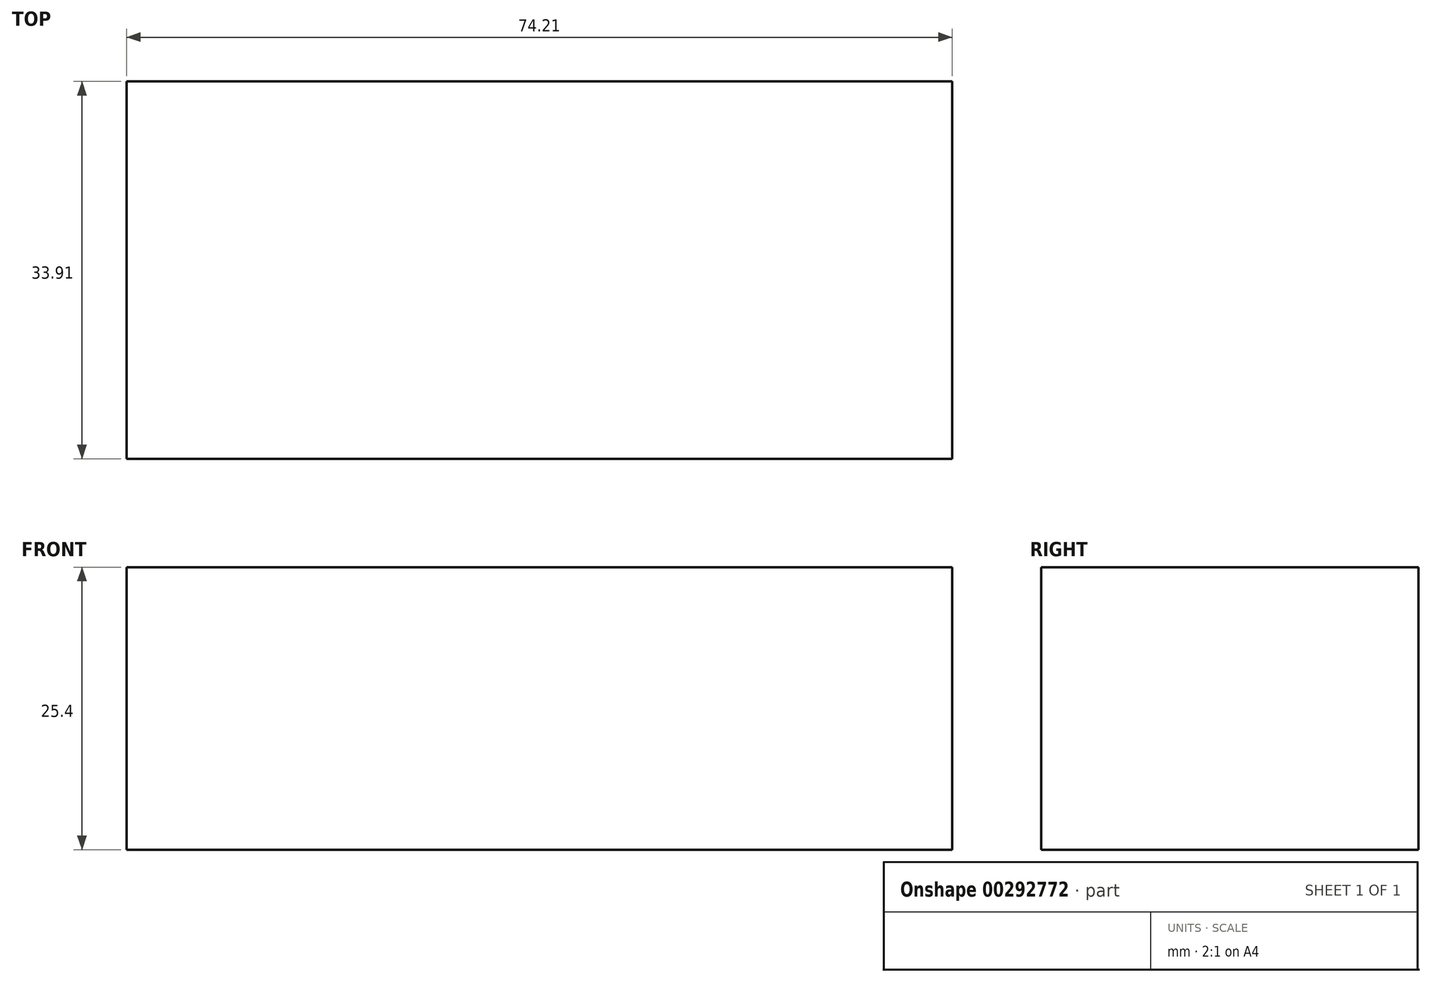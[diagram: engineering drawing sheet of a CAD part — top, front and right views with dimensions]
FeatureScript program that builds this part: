
annotation { "Feature Type Name" : "Feature", "Feature Type Description" : "" }
export const myFeature = defineFeature(function(context is Context, id is Id, definition is map)
    precondition{}
    {
        {
            var Q0;
            Q0=qCreatedBy(makeId("Top.planeOp"),FACE);
            var sketch = newSketch(context, id + "F0", { "sketchPlane" : qUnion([Q0])});
            skLineSegment(sketch, "E0.bottom", {"start": v(-23.48, -15.07) * mm, "end": v(50.73, -15.07) * mm});
            skLineSegment(sketch, "E0.top", {"start": v(-23.48, 18.84) * mm, "end": v(50.73, 18.84) * mm});
            skLineSegment(sketch, "E0.left", {"start": v(-23.48, -15.07) * mm, "end": v(-23.48, 18.84) * mm});
            skLineSegment(sketch, "E0.right", {"start": v(50.73, -15.07) * mm, "end": v(50.73, 18.84) * mm});
            skSolve(sketch);
        }
        {
            var Q0;
            Q0 = qSketchRegion(id + "F0", true);
            extrude(context, id + "F1", {"entities" : qUnion([Q0]), "depth" : 25.4 * mm});
        }
    });
